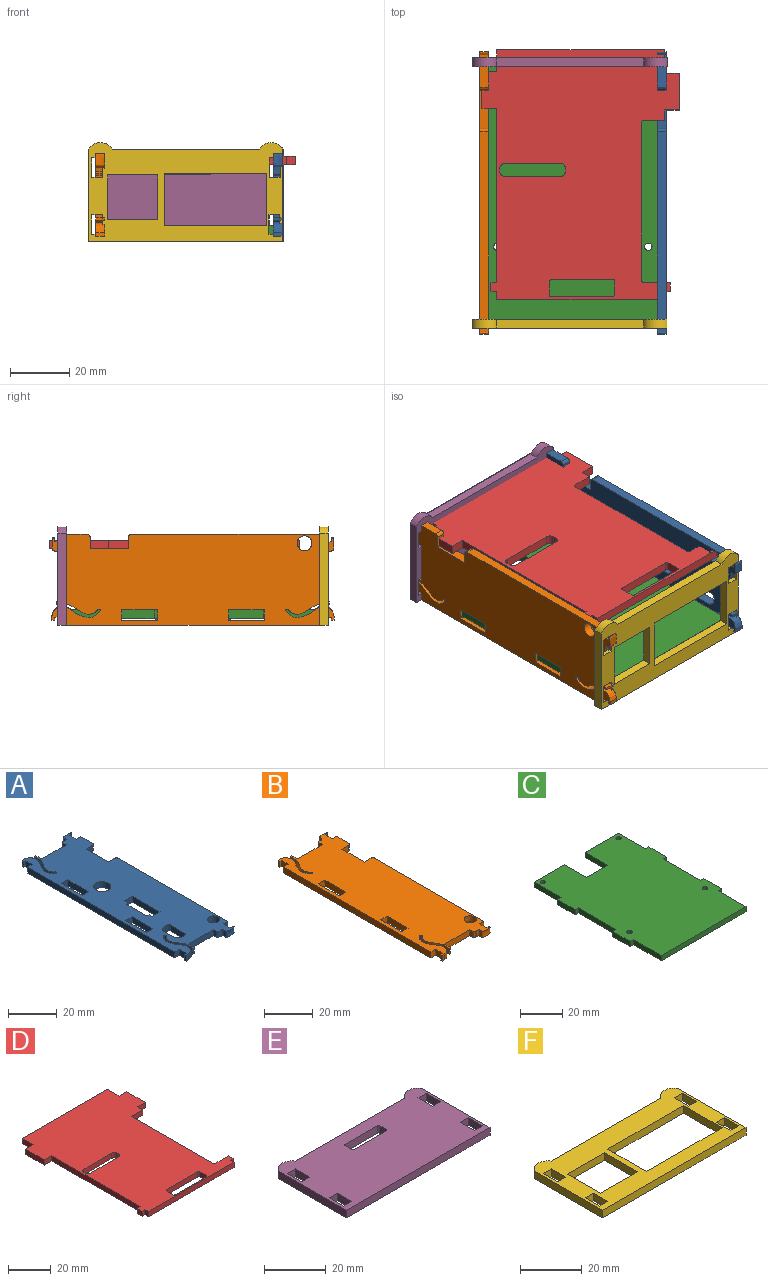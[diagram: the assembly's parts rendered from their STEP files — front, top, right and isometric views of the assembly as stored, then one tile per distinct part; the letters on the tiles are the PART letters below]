
ASSEMBLY  parts=6 mates=15
PART A: 64 faces, bbox 30.7x95.3x3 mm
  f0: plane 8.47x3mm, normal (-1,0,0), area 25.4mm2, adj f1,f61,f62,f63
  f1: cylinder r=2.04mm len=3mm, axis (0,0,-1), area 6.8mm2, adj f0,f2,f62,f63
  f2: cylinder r=3.41mm len=3.24mm, axis (0,0,-1), area 12.1mm2, adj f1,f3,f62,f63
  f3: plane 6.46x3mm, normal (1,0,0), area 19.4mm2, adj f2,f4,f62,f63
  f4: cylinder r=3.41mm len=3.24mm, axis (0,0,-1), area 12.1mm2, adj f3,f61,f62,f63
  f5: extruded ~16.27x3.55mm, area 61mm2, adj f6,f55,f62,f63
  f6: extruded ~11.3x3.16mm, area 38.2mm2, adj f5,f7,f62,f63
  f7: plane 3.37x3mm, normal (-1,0.01,0), area 10.1mm2, adj f6,f8,f62,f63
  f8: plane 3x0.8mm, normal (-0.01,-1,0), area 2.4mm2, adj f7,f9,f62,f63
  f9: plane 3.38x3mm, normal (1,-0.01,0), area 10.1mm2, adj f8,f10,f62,f63
  f10: plane 14.39x3mm, normal (0,-1,0), area 43.2mm2, adj f9,f11,f62,f63
  f11: plane 3x1.93mm, normal (-1,0,0), area 5.8mm2, adj f10,f12,f62,f63
  f12: extruded ~7.48x3mm, area 33.9mm2, adj f11,f13,f62,f63
  f13: plane 3.96x3mm, normal (1,0,0), area 11.9mm2, adj f12,f14,f62,f63
  f14: plane 3x2.54mm, normal (0,-1,0), area 7.6mm2, adj f13,f15,f62,f63
  f15: plane 63.38x3mm, normal (1,0,0), area 190.1mm2, adj f14,f16,f62,f63
  f16: cylinder r=1mm len=3mm, axis (0,0,-1), area 4.7mm2, adj f15,f17,f62,f63
  f17: plane 3.72x3mm, normal (0,1,0), area 11.2mm2, adj f16,f18,f62,f63
  f18: plane 12.95x3mm, normal (1,0,0), area 38.9mm2, adj f17,f19,f62,f63
  f19: plane 3.72x3mm, normal (0,-1,0), area 11.2mm2, adj f18,f20,f62,f63
  f20: cylinder r=1mm len=3mm, axis (0,0,-1), area 4.7mm2, adj f19,f21,f62,f63
  f21: plane 6.93x3mm, normal (1,0,0), area 20.8mm2, adj f20,f22,f62,f63
  f22: plane 3x2.54mm, normal (0,1,0), area 7.6mm2, adj f21,f23,f62,f63
  f23: plane 3.96x3mm, normal (1,0,0), area 11.9mm2, adj f22,f24,f62,f63
  f24: extruded ~7.47x3mm, area 34.3mm2, adj f23,f25,f62,f63
  f25: plane 3x1.93mm, normal (-1,0,0), area 5.8mm2, adj f24,f26,f62,f63
  f26: plane 14.18x3mm, normal (0,1,0), area 42.5mm2, adj f25,f27,f62,f63
  f27: plane 3.38x3mm, normal (1,0.01,0), area 10.1mm2, adj f26,f28,f62,f63
  f28: plane 3x0.8mm, normal (-0.01,1,0), area 2.4mm2, adj f27,f29,f62,f63
  f29: plane 3.37x3mm, normal (-1,-0.01,0), area 10.1mm2, adj f28,f30,f62,f63
  f30: extruded ~11.3x3.36mm, area 38.2mm2, adj f29,f31,f62,f63
  f31: extruded ~16.27x3.76mm, area 60.6mm2, adj f30,f32,f62,f63
  f32: plane 3x1.49mm, normal (0,1,0), area 4.5mm2, adj f31,f33,f62,f63
  f33: plane 3x1mm, normal (-1,0,0), area 3mm2, adj f32,f34,f62,f63
  f34: plane 3x1mm, normal (0,-1,0), area 3mm2, adj f33,f35,f62,f63
  f35: plane 3.97x3mm, normal (-1,0,0), area 11.9mm2, adj f34,f36,f62,f63
  f36: plane 3x2.69mm, normal (0,1,0), area 8.1mm2, adj f35,f37,f62,f63
  f37: plane 85.26x3mm, normal (-1,0,0), area 255.8mm2, adj f36,f38,f62,f63
  f38: plane 3x2.69mm, normal (0,-1,0), area 8.1mm2, adj f37,f39,f62,f63
  f39: plane 3.97x3mm, normal (-1,0,0), area 11.9mm2, adj f38,f40,f62,f63
  f40: plane 3x1mm, normal (0,1,0), area 3mm2, adj f39,f41,f62,f63
  f41: plane 3x1mm, normal (-1,0,0), area 3mm2, adj f40,f55,f62,f63
  f42: plane 12.06x3mm, normal (1,0,0), area 36.2mm2, adj f43,f56,f62,f63
  f43: plane 3.71x3mm, normal (0,-1,0), area 11.1mm2, adj f42,f44,f62,f63
  f44: plane 12.06x3mm, normal (-1,0,0), area 36.2mm2, adj f43,f56,f62,f63
  f45: plane 12.06x3mm, normal (1,0,0), area 36.2mm2, adj f46,f57,f62,f63
  f46: plane 3.71x3mm, normal (0,-1,0), area 11.1mm2, adj f45,f47,f62,f63
  f47: plane 12.06x3mm, normal (-1,0,0), area 36.2mm2, adj f46,f57,f62,f63
  f48: plane 10.78x3mm, normal (1,0,0), area 32.3mm2, adj f49,f58,f62,f63
  f49: plane 3x1.14mm, normal (0.61,-0.79,0), area 4.3mm2, adj f48,f50,f62,f63
  f50: plane 3x1.66mm, normal (1,0,0), area 5mm2, adj f49,f51,f62,f63
  f51: plane 4.71x3mm, normal (0,-1,0), area 14.1mm2, adj f50,f52,f62,f63
  f52: plane 15.88x3mm, normal (-1,0,0), area 47.6mm2, adj f51,f53,f62,f63
  f53: plane 4.71x3mm, normal (0,1,0), area 14.1mm2, adj f52,f54,f62,f63
  f54: plane 3x1.66mm, normal (1,0,0), area 5mm2, adj f53,f58,f62,f63
  f55: plane 3x1.28mm, normal (0,-1,0), area 3.8mm2, adj f5,f41,f62,f63
  f56: plane 3.71x3mm, normal (0,1,0), area 11.1mm2, adj f42,f44,f62,f63
  f57: plane 3.71x3mm, normal (0,1,0), area 11.1mm2, adj f45,f47,f62,f63
  f58: plane 3x1.14mm, normal (0.61,0.79,0), area 4.3mm2, adj f48,f54,f62,f63
  f59: cylinder r=2.5mm len=5mm, axis (0,0,-1), area 47.1mm2, adj f62,f63
  f60: cylinder r=3.5mm len=7mm, axis (0,0,-1), area 66mm2, adj f62,f63
  f61: cylinder r=2.04mm len=3mm, axis (0,0,-1), area 6.8mm2, adj f0,f4,f62,f63
  f62: plane 95.27x30.71mm, normal (0,0,1), area 2327.3mm2, adj f0,f1,f2,f3,f4,f5,f6,f7
  f63: plane 95.27x30.71mm, normal (0,0,-1), area 2327.3mm2, adj f0,f1,f2,f3,f4,f5,f6,f7
PART B: 53 faces, bbox 30.7x95.3x3 mm
  f0: extruded ~16.27x3.56mm, area 60.4mm2, adj f1,f50,f51,f52
  f1: extruded ~11.3x3.36mm, area 38.2mm2, adj f0,f2,f51,f52
  f2: plane 3.37x3mm, normal (-1,0.01,0), area 10.1mm2, adj f1,f3,f51,f52
  f3: plane 3x0.8mm, normal (-0.01,-1,0), area 2.4mm2, adj f2,f4,f51,f52
  f4: plane 3.38x3mm, normal (1,-0.01,0), area 10.1mm2, adj f3,f5,f51,f52
  f5: plane 14.39x3mm, normal (0,-1,0), area 43.2mm2, adj f4,f6,f51,f52
  f6: plane 3x1.93mm, normal (-1,0,0), area 5.8mm2, adj f5,f7,f51,f52
  f7: extruded ~3x0.69mm, area 3.3mm2, adj f6,f8,f51,f52
  f8: plane 3x0.74mm, normal (0,-1,0), area 2.2mm2, adj f7,f9,f51,f52
  f9: extruded ~5.85x3mm, area 27.4mm2, adj f8,f10,f51,f52
  f10: plane 3.96x3mm, normal (1,0,0), area 11.9mm2, adj f9,f11,f51,f52
  f11: plane 3x2.54mm, normal (0,-1,0), area 7.6mm2, adj f10,f12,f51,f52
  f12: plane 63.38x3mm, normal (1,0,0), area 190.1mm2, adj f11,f13,f51,f52
  f13: cylinder r=1mm len=3mm, axis (0,0,-1), area 4.7mm2, adj f12,f14,f51,f52
  f14: plane 3.93x3mm, normal (0,1,0), area 11.8mm2, adj f13,f15,f51,f52
  f15: plane 12.95x3mm, normal (1,0,0), area 38.9mm2, adj f14,f16,f51,f52
  f16: plane 3.93x3mm, normal (0,-1,0), area 11.8mm2, adj f15,f17,f51,f52
  f17: cylinder r=1mm len=3mm, axis (0,0,-1), area 4.7mm2, adj f16,f18,f51,f52
  f18: plane 6.93x3mm, normal (1,0,0), area 20.8mm2, adj f17,f19,f51,f52
  f19: plane 3x2.54mm, normal (0,1,0), area 7.6mm2, adj f18,f20,f51,f52
  f20: plane 3.96x3mm, normal (1,0,0), area 11.9mm2, adj f19,f21,f51,f52
  f21: extruded ~5.85x3mm, area 27.4mm2, adj f20,f22,f51,f52
  f22: plane 3x0.74mm, normal (0,1,0), area 2.2mm2, adj f21,f23,f51,f52
  f23: extruded ~3x0.69mm, area 3.3mm2, adj f22,f24,f51,f52
  f24: plane 3x1.93mm, normal (-1,0,0), area 5.8mm2, adj f23,f25,f51,f52
  f25: plane 14.39x3mm, normal (0,1,0), area 43.2mm2, adj f24,f26,f51,f52
  f26: plane 3.38x3mm, normal (1,0.01,0), area 10.1mm2, adj f25,f27,f51,f52
  f27: plane 3x0.8mm, normal (-0.01,1,0), area 2.4mm2, adj f26,f28,f51,f52
  f28: plane 3.37x3mm, normal (-1,-0.01,0), area 10.1mm2, adj f27,f29,f51,f52
  f29: extruded ~11.3x3.36mm, area 38.2mm2, adj f28,f30,f51,f52
  f30: extruded ~16.27x3.56mm, area 60.4mm2, adj f29,f31,f51,f52
  f31: plane 3x1.28mm, normal (0,1,0), area 3.8mm2, adj f30,f32,f51,f52
  f32: plane 3x1mm, normal (-1,0,0), area 3mm2, adj f31,f33,f51,f52
  f33: plane 3x1mm, normal (0,-1,0), area 3mm2, adj f32,f34,f51,f52
  f34: plane 3.97x3mm, normal (-1,0,0), area 11.9mm2, adj f33,f35,f51,f52
  f35: plane 3x2.69mm, normal (0,1,0), area 8.1mm2, adj f34,f36,f51,f52
  f36: plane 85.26x3mm, normal (-1,0,0), area 255.8mm2, adj f35,f37,f51,f52
  f37: plane 3x2.69mm, normal (0,-1,0), area 8.1mm2, adj f36,f38,f51,f52
  f38: plane 3.97x3mm, normal (-1,0,0), area 11.9mm2, adj f37,f39,f51,f52
  f39: plane 3x1mm, normal (0,1,0), area 3mm2, adj f38,f40,f51,f52
  f40: plane 3x1mm, normal (-1,0,0), area 3mm2, adj f39,f50,f51,f52
  f41: plane 12.06x3mm, normal (1,0,0), area 36.2mm2, adj f42,f47,f51,f52
  f42: plane 3.71x3mm, normal (0,-1,0), area 11.1mm2, adj f41,f43,f51,f52
  f43: plane 12.06x3mm, normal (-1,0,0), area 36.2mm2, adj f42,f47,f51,f52
  f44: plane 12.06x3mm, normal (1,0,0), area 36.2mm2, adj f45,f48,f51,f52
  f45: plane 3.71x3mm, normal (0,-1,0), area 11.1mm2, adj f44,f46,f51,f52
  f46: plane 12.06x3mm, normal (-1,0,0), area 36.2mm2, adj f45,f48,f51,f52
  f47: plane 3.71x3mm, normal (0,1,0), area 11.1mm2, adj f41,f43,f51,f52
  f48: plane 3.71x3mm, normal (0,1,0), area 11.1mm2, adj f44,f46,f51,f52
  f49: cylinder r=2.5mm len=5mm, axis (0,0,-1), area 47.1mm2, adj f51,f52
  f50: plane 3x1.28mm, normal (0,-1,0), area 3.8mm2, adj f0,f40,f51,f52
  f51: plane 95.3x30.71mm, normal (0,0,1), area 2499.2mm2, adj f0,f1,f2,f3,f4,f5,f6,f7
  f52: plane 95.3x30.71mm, normal (0,0,-1), area 2499.2mm2, adj f0,f1,f2,f3,f4,f5,f6,f7
PART C: 30 faces, bbox 61.4x85.7x3 mm
  f0: plane 18.75x3mm, normal (1,0,0), area 56.2mm2, adj f1,f23,f28,f29
  f1: plane 3x2.24mm, normal (0,-1,0), area 6.7mm2, adj f0,f2,f28,f29
  f2: plane 11.79x3mm, normal (1,0,0), area 35.4mm2, adj f1,f3,f28,f29
  f3: plane 3x2.24mm, normal (0,1,0), area 6.7mm2, adj f2,f4,f28,f29
  f4: plane 25.2x3mm, normal (1,0,0), area 75.6mm2, adj f3,f5,f28,f29
  f5: plane 3x2.24mm, normal (0,-1,0), area 6.7mm2, adj f4,f6,f28,f29
  f6: plane 11.79x3mm, normal (1,0,0), area 35.4mm2, adj f5,f7,f28,f29
  f7: plane 3x2.24mm, normal (0,1,0), area 6.7mm2, adj f6,f8,f28,f29
  f8: plane 18.16x3mm, normal (1,0,0), area 54.5mm2, adj f7,f9,f28,f29
  f9: plane 22.3x3mm, normal (0,1,0), area 66.9mm2, adj f8,f10,f28,f29
  f10: plane 15.01x3mm, normal (-1,0,0), area 45mm2, adj f9,f11,f28,f29
  f11: plane 14.33x3mm, normal (0,1,0), area 43mm2, adj f10,f12,f28,f29
  f12: plane 15.01x3mm, normal (1,0,0), area 45mm2, adj f11,f13,f28,f29
  f13: plane 20.27x3mm, normal (0,1,0), area 60.8mm2, adj f12,f14,f28,f29
  f14: plane 18.16x3mm, normal (-1,0,0), area 54.5mm2, adj f13,f15,f28,f29
  f15: plane 3x2.24mm, normal (0,1,0), area 6.7mm2, adj f14,f16,f28,f29
  f16: plane 11.79x3mm, normal (-1,0,0), area 35.4mm2, adj f15,f17,f28,f29
  f17: plane 3x2.24mm, normal (0,-1,0), area 6.7mm2, adj f16,f18,f28,f29
  f18: plane 25.2x3mm, normal (-1,0,0), area 75.6mm2, adj f17,f19,f28,f29
  f19: plane 3x2.24mm, normal (0,1,0), area 6.7mm2, adj f18,f20,f28,f29
  f20: plane 11.79x3mm, normal (-1,0,0), area 35.4mm2, adj f19,f21,f28,f29
  f21: plane 3x2.24mm, normal (0,-1,0), area 6.7mm2, adj f20,f22,f28,f29
  f22: plane 18.75x3mm, normal (-1,0,0), area 56.2mm2, adj f21,f23,f28,f29
  f23: plane 56.9x3mm, normal (0,-1,0), area 170.7mm2, adj f0,f22,f28,f29
  f24: cylinder r=1.26mm len=3mm, axis (0,0,-1), area 23.7mm2, adj f28,f29
  f25: cylinder r=1.26mm len=3mm, axis (0,0,-1), area 23.7mm2, adj f28,f29
  f26: cylinder r=1.26mm len=3mm, axis (0,0,-1), area 23.7mm2, adj f28,f29
  f27: cylinder r=1.26mm len=3mm, axis (0,0,-1), area 23.7mm2, adj f28,f29
  f28: plane 85.67x61.37mm, normal (0,0,1), area 4745mm2, adj f0,f1,f2,f3,f4,f5,f6,f7
  f29: plane 85.67x61.37mm, normal (0,0,-1), area 4745mm2, adj f0,f1,f2,f3,f4,f5,f6,f7
PART D: 42 faces, bbox 66.6x84.1x3 mm
  f0: plane 20.65x3mm, normal (0,1,0), area 61.9mm2, adj f1,f39,f40,f41
  f1: cylinder r=0.7mm len=3mm, axis (0,0,-1), area 2.6mm2, adj f0,f2,f40,f41
  f2: plane 4.67x3mm, normal (1,0,0), area 14mm2, adj f1,f3,f40,f41
  f3: cylinder r=0.7mm len=3mm, axis (0,0,-1), area 3.3mm2, adj f2,f4,f40,f41
  f4: plane 20.65x3mm, normal (0,-1,0), area 61.9mm2, adj f3,f5,f40,f41
  f5: cylinder r=0.7mm len=3mm, axis (0,0,-1), area 2.6mm2, adj f4,f6,f40,f41
  f6: plane 4.67x3mm, normal (-1,0,0), area 14mm2, adj f5,f39,f40,f41
  f7: plane 3x2.59mm, normal (1,0,0), area 7.8mm2, adj f8,f37,f40,f41
  f8: plane 3x1.97mm, normal (0,-1,0), area 5.9mm2, adj f7,f9,f40,f41
  f9: plane 3x3mm, normal (1,0.01,0), area 9mm2, adj f8,f10,f40,f41
  f10: plane 9.06x3mm, normal (0,1,0), area 27.2mm2, adj f9,f11,f40,f41
  f11: cylinder r=0.51mm len=3mm, axis (0,0,-1), area 2.4mm2, adj f10,f12,f40,f41
  f12: plane 53.85x3mm, normal (1,0,0), area 161.5mm2, adj f11,f13,f40,f41
  f13: cylinder r=0.5mm len=3mm, axis (0,0,-1), area 2.4mm2, adj f12,f14,f40,f41
  f14: plane 7.13x3mm, normal (0,-1,0), area 21.4mm2, adj f13,f15,f40,f41
  f15: plane 3.4x3mm, normal (1,0,0), area 10.2mm2, adj f14,f16,f40,f41
  f16: plane 4.96x3mm, normal (0,-1,0), area 14.9mm2, adj f15,f17,f40,f41
  f17: plane 12.42x3mm, normal (1,0,0), area 37.3mm2, adj f16,f18,f40,f41
  f18: plane 4.96x3mm, normal (0,1,0), area 14.9mm2, adj f17,f19,f40,f41
  f19: plane 7.88x3mm, normal (1,0,0), area 23.6mm2, adj f18,f20,f40,f41
  f20: plane 56.64x3mm, normal (0,1,0), area 169.9mm2, adj f19,f21,f40,f41
  f21: plane 7.35x3mm, normal (-1,0,0), area 22mm2, adj f20,f22,f40,f41
  f22: plane 4.96x3mm, normal (0,1,0), area 14.9mm2, adj f21,f23,f40,f41
  f23: plane 12.42x3mm, normal (-1,0,0), area 37.3mm2, adj f22,f24,f40,f41
  f24: plane 4.96x3mm, normal (0,-1,0), area 14.9mm2, adj f23,f25,f40,f41
  f25: plane 58.86x3mm, normal (-1,0,0), area 176.6mm2, adj f24,f26,f40,f41
  f26: plane 3x1.93mm, normal (0,1,0), area 5.8mm2, adj f25,f27,f40,f41
  f27: plane 3x3mm, normal (-1,0,0), area 9mm2, adj f26,f28,f40,f41
  f28: plane 3x1.93mm, normal (0,-1,0), area 5.8mm2, adj f27,f29,f40,f41
  f29: plane 3x2.52mm, normal (-1,0,0), area 7.6mm2, adj f28,f37,f40,f41
  f30: plane 18.59x3mm, normal (0,1,0), area 55.8mm2, adj f31,f38,f40,f41
  f31: cylinder r=1.78mm len=3mm, axis (0,0,-1), area 8.4mm2, adj f30,f32,f40,f41
  f32: plane 3x0.91mm, normal (1,0,0), area 2.7mm2, adj f31,f33,f40,f41
  f33: cylinder r=1.78mm len=3mm, axis (0,0,-1), area 8.4mm2, adj f32,f34,f40,f41
  f34: plane 18.59x3mm, normal (0,-1,0), area 55.8mm2, adj f33,f35,f40,f41
  f35: cylinder r=1.78mm len=3mm, axis (0,0,-1), area 8.4mm2, adj f34,f36,f40,f41
  f36: plane 3x0.91mm, normal (-1,0,0), area 2.7mm2, adj f35,f38,f40,f41
  f37: plane 56.64x3mm, normal (0,-1,0), area 169.9mm2, adj f7,f29,f40,f41
  f38: cylinder r=1.78mm len=3mm, axis (0,0,-1), area 8.4mm2, adj f30,f36,f40,f41
  f39: cylinder r=0.7mm len=3mm, axis (0,0,-1), area 3.3mm2, adj f0,f6,f40,f41
  f40: plane 84.15x66.56mm, normal (0,0,1), area 4259.8mm2, adj f0,f1,f2,f3,f4,f5,f6,f7
  f41: plane 84.15x66.56mm, normal (0,0,-1), area 4259.8mm2, adj f0,f1,f2,f3,f4,f5,f6,f7
PART E: 32 faces, bbox 65.5x33.4x3 mm
  f0: plane 6.53x3mm, normal (-1,0,0), area 19.6mm2, adj f1,f29,f30,f31
  f1: plane 3.7x3mm, normal (0,1,0), area 11.1mm2, adj f0,f2,f30,f31
  f2: plane 6.53x3mm, normal (1,0,0), area 19.6mm2, adj f1,f29,f30,f31
  f3: plane 31.17x3mm, normal (1,0,0), area 93.5mm2, adj f4,f24,f30,f31
  f4: cylinder r=4.62mm len=7.85mm, axis (0,0,-1), area 28.1mm2, adj f3,f5,f30,f31
  f5: plane 49.78x3mm, normal (0,1,0), area 149.3mm2, adj f4,f6,f30,f31
  f6: cylinder r=4.62mm len=7.85mm, axis (0,0,-1), area 28.1mm2, adj f5,f7,f30,f31
  f7: plane 31.17x3mm, normal (-1,0,0), area 93.5mm2, adj f6,f24,f30,f31
  f8: plane 3.7x3mm, normal (0,1,0), area 11.1mm2, adj f9,f25,f30,f31
  f9: plane 6.53x3mm, normal (1,0,0), area 19.6mm2, adj f8,f10,f30,f31
  f10: plane 3.7x3mm, normal (0,-1,0), area 11.1mm2, adj f9,f25,f30,f31
  f11: plane 3.7x3mm, normal (0,1,0), area 11.1mm2, adj f12,f26,f30,f31
  f12: plane 6.53x3mm, normal (1,0,0), area 19.6mm2, adj f11,f13,f30,f31
  f13: plane 3.7x3mm, normal (0,-1,0), area 11.1mm2, adj f12,f26,f30,f31
  f14: plane 3.7x3mm, normal (0,-1,0), area 11.1mm2, adj f15,f27,f30,f31
  f15: plane 6.53x3mm, normal (-1,0,0), area 19.6mm2, adj f14,f16,f30,f31
  f16: plane 3.7x3mm, normal (0,1,0), area 11.1mm2, adj f15,f27,f30,f31
  f17: plane 3.07x3mm, normal (1,0,0), area 9.2mm2, adj f18,f28,f30,f31
  f18: cylinder r=0.5mm len=3mm, axis (0,0,-1), area 2.4mm2, adj f17,f19,f30,f31
  f19: plane 14.85x3mm, normal (0,-1,0), area 44.5mm2, adj f18,f20,f30,f31
  f20: cylinder r=0.5mm len=3mm, axis (0,0,-1), area 2.4mm2, adj f19,f21,f30,f31
  f21: plane 3.07x3mm, normal (-1,0,0), area 9.2mm2, adj f20,f22,f30,f31
  f22: cylinder r=0.5mm len=3mm, axis (0,0,-1), area 2.4mm2, adj f21,f23,f30,f31
  f23: plane 14.85x3mm, normal (0,1,0), area 44.5mm2, adj f22,f28,f30,f31
  f24: plane 65.48x3mm, normal (0,-1,0), area 196.4mm2, adj f3,f7,f30,f31
  f25: plane 6.53x3mm, normal (-1,0,0), area 19.6mm2, adj f8,f10,f30,f31
  f26: plane 6.53x3mm, normal (-1,0,0), area 19.6mm2, adj f11,f13,f30,f31
  f27: plane 6.53x3mm, normal (1,0,0), area 19.6mm2, adj f14,f16,f30,f31
  f28: cylinder r=0.5mm len=3mm, axis (0,0,-1), area 2.4mm2, adj f17,f23,f30,f31
  f29: plane 3.7x3mm, normal (0,-1,0), area 11.1mm2, adj f0,f2,f30,f31
  f30: plane 65.48x33.35mm, normal (0,0,1), area 1904.2mm2, adj f0,f1,f2,f3,f4,f5,f6,f7
  f31: plane 65.48x33.35mm, normal (0,0,-1), area 1904.2mm2, adj f0,f1,f2,f3,f4,f5,f6,f7
PART F: 32 faces, bbox 65.5x33.4x3 mm
  f0: plane 6.53x3mm, normal (-1,0,0), area 19.6mm2, adj f1,f29,f30,f31
  f1: plane 3.7x3mm, normal (0,1,0), area 11.1mm2, adj f0,f2,f30,f31
  f2: plane 6.53x3mm, normal (1,0,0), area 19.6mm2, adj f1,f29,f30,f31
  f3: plane 31.17x3mm, normal (1,0,0), area 93.5mm2, adj f4,f23,f30,f31
  f4: cylinder r=4.62mm len=7.85mm, axis (0,0,-1), area 28.1mm2, adj f3,f5,f30,f31
  f5: plane 49.78x3mm, normal (0,1,0), area 149.3mm2, adj f4,f6,f30,f31
  f6: cylinder r=4.62mm len=7.85mm, axis (0,0,-1), area 28.1mm2, adj f5,f7,f30,f31
  f7: plane 31.17x3mm, normal (-1,0,0), area 93.5mm2, adj f6,f23,f30,f31
  f8: plane 3.7x3mm, normal (0,1,0), area 11.1mm2, adj f9,f24,f30,f31
  f9: plane 6.53x3mm, normal (1,0,0), area 19.6mm2, adj f8,f10,f30,f31
  f10: plane 3.7x3mm, normal (0,-1,0), area 11.1mm2, adj f9,f24,f30,f31
  f11: plane 3.7x3mm, normal (0,1,0), area 11.1mm2, adj f12,f25,f30,f31
  f12: plane 6.53x3mm, normal (1,0,0), area 19.6mm2, adj f11,f13,f30,f31
  f13: plane 3.7x3mm, normal (0,-1,0), area 11.1mm2, adj f12,f25,f30,f31
  f14: plane 16.9x3mm, normal (0,1,0), area 50.7mm2, adj f15,f26,f30,f31
  f15: plane 15.12x3mm, normal (1,0,0), area 45.4mm2, adj f14,f16,f30,f31
  f16: plane 16.9x3mm, normal (0,-1,0), area 50.7mm2, adj f15,f26,f30,f31
  f17: plane 34.6x3mm, normal (0,1,0), area 103.8mm2, adj f18,f27,f30,f31
  f18: plane 17.7x3mm, normal (1,0,0), area 53.1mm2, adj f17,f19,f30,f31
  f19: plane 34.6x3mm, normal (0,-1,0), area 103.8mm2, adj f18,f27,f30,f31
  f20: plane 3.7x3mm, normal (0,-1,0), area 11.1mm2, adj f21,f28,f30,f31
  f21: plane 6.53x3mm, normal (-1,0,0), area 19.6mm2, adj f20,f22,f30,f31
  f22: plane 3.7x3mm, normal (0,1,0), area 11.1mm2, adj f21,f28,f30,f31
  f23: plane 65.48x3mm, normal (0,-1,0), area 196.4mm2, adj f3,f7,f30,f31
  f24: plane 6.53x3mm, normal (-1,0,0), area 19.6mm2, adj f8,f10,f30,f31
  f25: plane 6.53x3mm, normal (-1,0,0), area 19.6mm2, adj f11,f13,f30,f31
  f26: plane 15.12x3mm, normal (-1,0,0), area 45.4mm2, adj f14,f16,f30,f31
  f27: plane 17.7x3mm, normal (-1,0,0), area 53.1mm2, adj f17,f19,f30,f31
  f28: plane 6.53x3mm, normal (1,0,0), area 19.6mm2, adj f20,f22,f30,f31
  f29: plane 3.7x3mm, normal (0,-1,0), area 11.1mm2, adj f0,f2,f30,f31
  f30: plane 65.48x33.35mm, normal (0,0,1), area 1100.5mm2, adj f0,f1,f2,f3,f4,f5,f6,f7
  f31: plane 65.48x33.35mm, normal (0,0,-1), area 1100.5mm2, adj f0,f1,f2,f3,f4,f5,f6,f7
PLACE A rot(axis=(0,-1,0),90deg) t=(3.98,-17.66,99.8)mm
PLACE B rot(axis=(0,-1,0),90deg) t=(-55.91,-7.8,79.68)mm
PLACE C t=(-30.81,80.12,69.09)mm
PLACE D t=(-39.14,14.36,92.57)mm
PLACE E rot(axis=(1,0,0),90deg) t=(-29.05,40.03,84.84)mm
PLACE F rot(axis=(1,0,0),90deg) t=(-32.54,-48.23,88.33)mm
MATE planar D.f41 <-> B.f15  axis (0,0,-1) through (-58.15,29.13,92.57)mm
MATE planar A.f44 <-> C.f28  axis (0,0,-1) through (2.48,-24.26,72.09)mm
MATE planar B.f46 <-> C.f28  axis (0,0,-1) through (-57.41,12.41,72.09)mm
MATE planar F.f29 <-> A.f13  axis (0,0,-1) through (1.49,-49.73,94.95)mm
MATE planar A.f62 <-> C.f8  axis (-1,0,0) through (0.98,-5.6,66.78)mm
MATE parallel F.f30 <-> C.f23  axis (0,-1,0) through (-28.48,-51.23,97.95)mm
MATE parallel E.f31 <-> F.f30  axis (0,1,0) through (-28.46,40.03,82.29)mm
MATE planar E.f29 <-> A.f23  axis (0,0,-1) through (1.43,38.53,94.95)mm
MATE planar B.f52 <-> C.f18  axis (1,0,0) through (-55.91,-6.03,82.3)mm
MATE planar E.f30 <-> B.f25  axis (0,-1,0) through (-28.46,37.03,82.29)mm
MATE parallel A.f62 <-> C.f8  axis (-1,0,0) through (0.98,16.16,92.77)mm
MATE planar B.f37 <-> C.f23  axis (0,-1,0) through (-57.41,-48.23,68.13)mm
MATE planar F.f31 <-> A.f14  axis (0,1,0) through (-3.59,-48.23,97.95)mm
MATE planar A.f10 <-> C.f23  axis (0,-1,0) through (2.48,-48.23,74.72)mm
MATE parallel B.f51 <-> C.f18  axis (-1,0,0) through (-58.91,-6.03,82.3)mm
